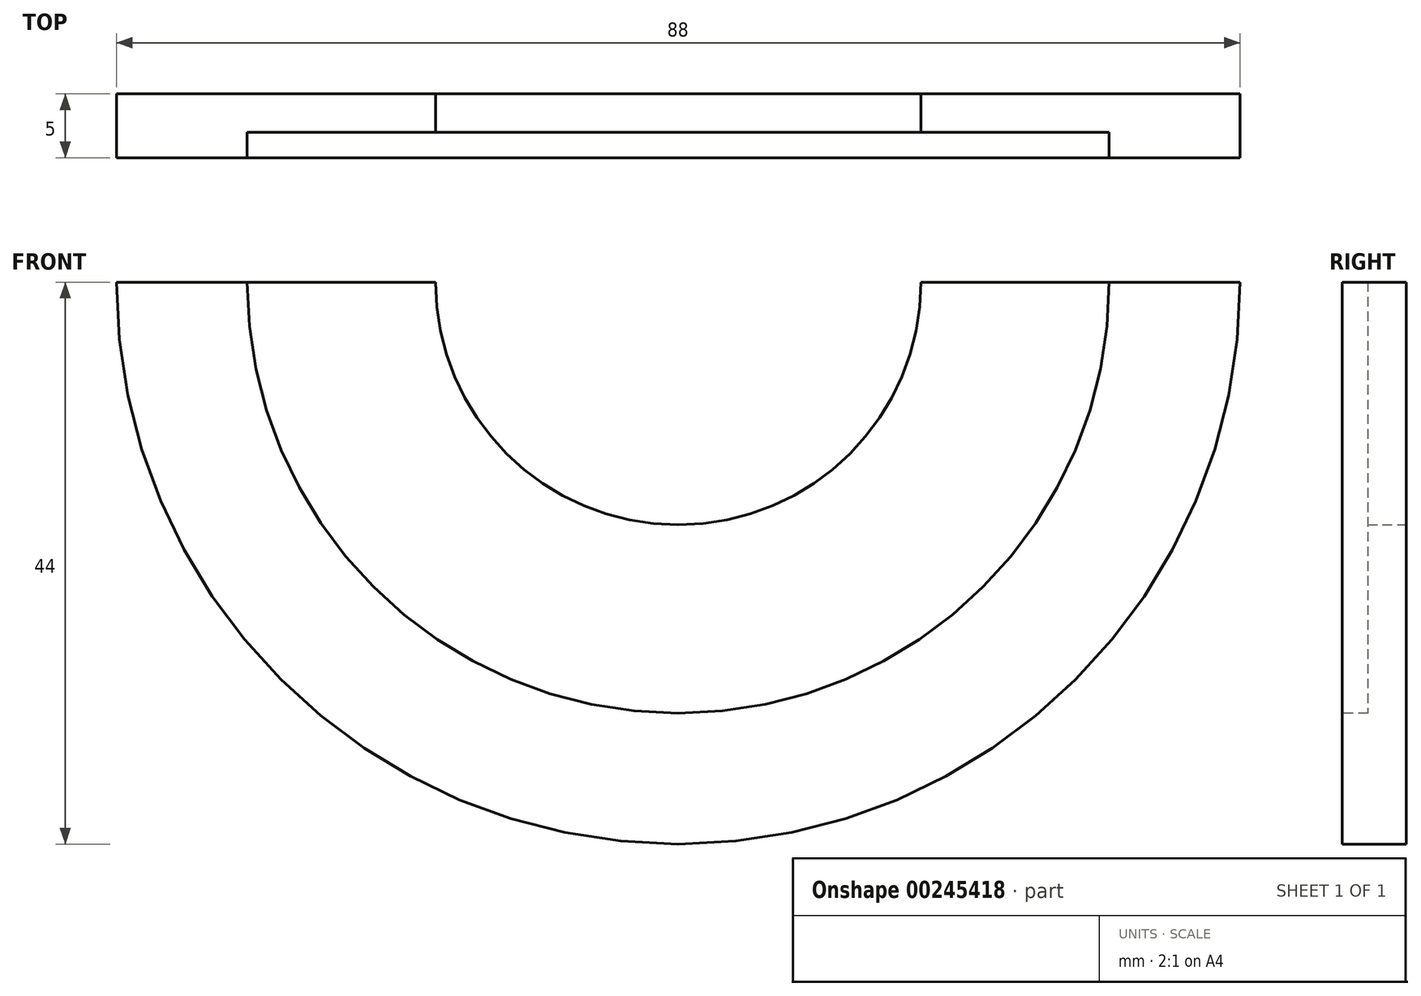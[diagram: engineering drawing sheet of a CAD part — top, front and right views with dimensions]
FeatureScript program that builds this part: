
annotation { "Feature Type Name" : "Feature", "Feature Type Description" : "" }
export const myFeature = defineFeature(function(context is Context, id is Id, definition is map)
    precondition{}
    {
        {
            var Q0;
            Q0=qCreatedBy(makeId("Front.planeOp"),FACE);
            var sketch = newSketch(context, id + "F0", { "sketchPlane" : qUnion([Q0])});
            skCircle(sketch, "E0", {"center": v(0, 0) * mm, "radius": 19 * mm});
            skCircle(sketch, "E1", {"center": v(0, 0) * mm, "radius": 44 * mm});
            skSolve(sketch);
        }
        {
            var Q0;
            Q0 = qSketchRegion(id + "F0", true);
            extrude(context, id + "F1", {"entities" : qUnion([Q0]), "depth" : 5 * mm});
        }
        {
            var Q0;
            Q0=makeQuery(id+"F1.opExtrude","CAP_FACE",FACE,{"disambiguationData":[OSD([sQuery(id+"F0.wireOp",EDGE,"E0"),sQuery(id+"F0.wireOp",EDGE,"E1")])],"isStart":false});
            var sketch = newSketch(context, id + "F2", { "sketchPlane" : qUnion([Q0])});
            skCircle(sketch, "E2", {"center": v(0, 0) * mm, "radius": 33.75 * mm});
            skSolve(sketch);
        }
        {
            var Q0;
            Q0 = qSketchRegion(id + "F2", true);
            extrude(context, id + "F3", {"entities" : qUnion([Q0]), "operationType" : NewBodyOperationType.REMOVE, "oppositeDirection" : true, "depth" : 2 * mm});
        }
        {
            var Q0;
            Q0=qCreatedBy(makeId("Front.planeOp"),FACE);
            var sketch = newSketch(context, id + "F4", { "sketchPlane" : qUnion([Q0])});
            skLineSegment(sketch, "E3", {"start": v(0, 0) * mm, "end": v(-49.32, 0) * mm});
            skLineSegment(sketch, "E4", {"start": v(-49.32, 0) * mm, "end": v(-49.32, 41.9) * mm});
            skLineSegment(sketch, "E5", {"start": v(-49.32, 41.9) * mm, "end": v(0, 51.78) * mm});
            skLineSegment(sketch, "E6", {"start": v(0, 51.78) * mm, "end": v(50.37, 35.83) * mm});
            skLineSegment(sketch, "E7", {"start": v(50.37, 35.83) * mm, "end": v(50.37, 0) * mm});
            skLineSegment(sketch, "E8", {"start": v(50.37, 0) * mm, "end": v(0, 0) * mm});
            skSolve(sketch);
        }
        {
            var Q0;
            Q0 = qSketchRegion(id + "F4", true);
            extrude(context, id + "F5", {"entities" : qUnion([Q0]), "operationType" : NewBodyOperationType.REMOVE, "depth" : 25 * mm});
        }
    });
